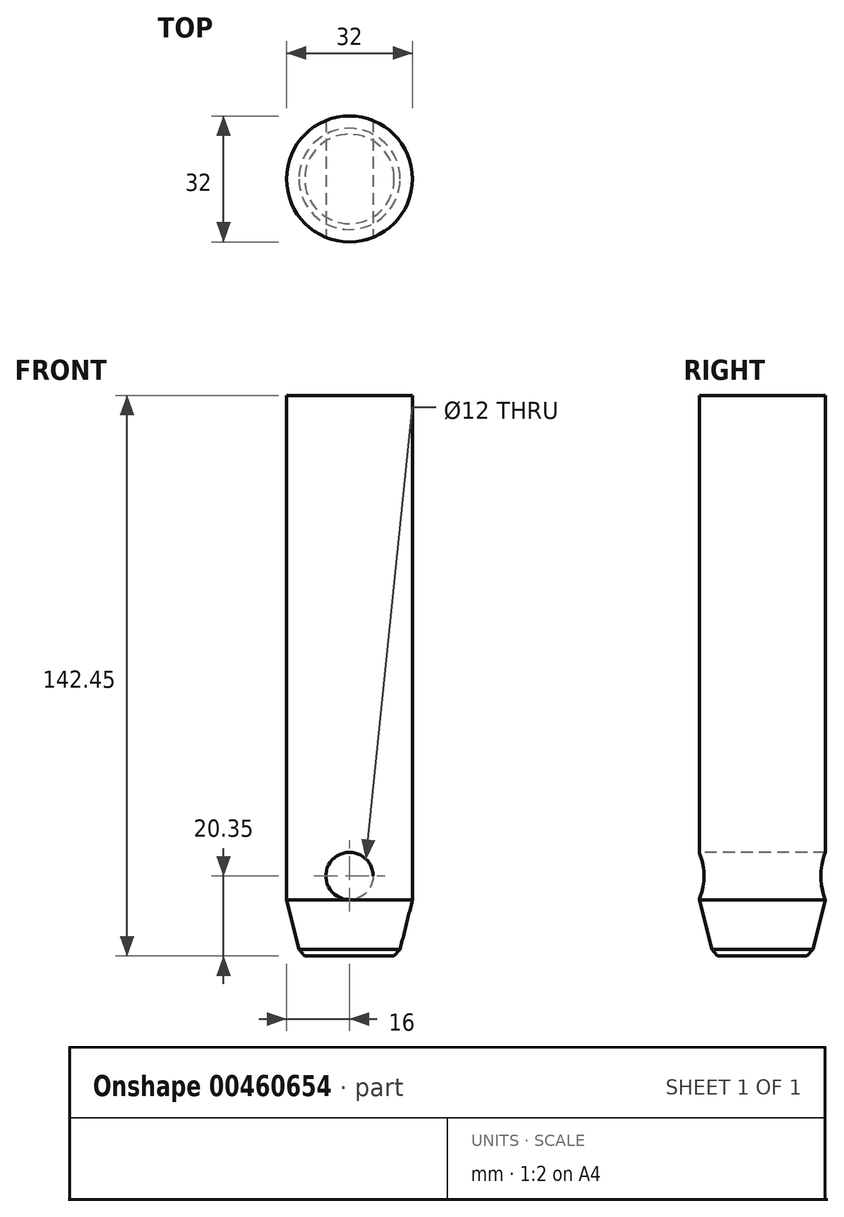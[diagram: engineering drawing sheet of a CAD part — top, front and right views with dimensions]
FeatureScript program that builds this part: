
annotation { "Feature Type Name" : "Feature", "Feature Type Description" : "" }
export const myFeature = defineFeature(function(context is Context, id is Id, definition is map)
    precondition{}
    {
        {
            var Q0;
            Q0=qCreatedBy(makeId("Front.planeOp"),FACE);
            var sketch = newSketch(context, id + "F0", { "sketchPlane" : qUnion([Q0])});
            skLineSegment(sketch, "E0.bottom", {"start": v(16, -71) * mm, "end": v(-16, -71) * mm});
            skLineSegment(sketch, "E0.top", {"start": v(16, 71) * mm, "end": v(-16, 71) * mm});
            skLineSegment(sketch, "E0.left", {"start": v(16, -71) * mm, "end": v(16, 71) * mm});
            skLineSegment(sketch, "E0.right", {"start": v(-16, -71) * mm, "end": v(-16, 71) * mm});
            skPoint(sketch, "E0.middle", {"position": v(0, 0) * mm});
            skLineSegment(sketch, "E1.0", {"start": v(16, -69.5) * mm, "end": v(-16, -69.5) * mm});
            skLineSegment(sketch, "E2.0", {"start": v(16, -57) * mm, "end": v(-16, -57) * mm});
            skLineSegment(sketch, "E3.0", {"start": v(16, -51) * mm, "end": v(-16, -51) * mm});
            skLineSegment(sketch, "E4", {"start": v(0, -49.32) * mm, "end": v(0, -53.2) * mm});
            skPoint(sketch, "E4.startSnap0", {"position": v(0, -51) * mm});
            skSolve(sketch);
        }
        {
            var Q0;
            Q0=qCreatedBy(makeId("Top.planeOp"),FACE);
            var sketch = newSketch(context, id + "F1", { "sketchPlane" : qUnion([Q0])});
            skCircle(sketch, "E5", {"center": v(0, 0) * mm, "radius": 16 * mm});
            skSolve(sketch);
        }
        {
            var Q0;
            Q0 = qSketchRegion(id + "F1", true);
            extrude(context, id + "F2", {"entities" : qUnion([Q0]), "depth" : 71.1 * mm});
        }
        {
            var Q0;
            Q0=makeQuery(id+"F2.opExtrude","CAP_FACE",FACE,{"disambiguationData":[OSD([sQuery(id+"F1.wireOp",EDGE,"E5")])],"isStart":true});
            extrude(context, id + "F3", {"entities" : qUnion([Q0]), "operationType" : NewBodyOperationType.ADD, "depth" : 57.1 * mm});
        }
        {
            var Q0;
            Q0=makeQuery(id+"F3.opExtrude","CAP_FACE",FACE,{"disambiguationData":[OSD([sQuery(id+"F1.wireOp",EDGE,"E5")])],"isStart":false});
            cPlane(context, id + "F4", {"entities" : qUnion([Q0]), "cplaneType" : CPlaneType.OFFSET, "offset" : 12.5 * mm, "width" : 150 * mm, "height" : 150 * mm});
        }
        {
            var Q0;
            Q0=qCreatedBy(id+"F4.planeOp",FACE);
            var sketch = newSketch(context, id + "F5", { "sketchPlane" : qUnion([Q0])});
            skCircle(sketch, "E6", {"center": v(0, 0) * mm, "radius": 12.85 * mm});
            skSolve(sketch);
        }
        {
            var Q1;
            Q1=makeQuery(id+"F3.opExtrude","CAP_FACE",FACE,{"disambiguationData":[OSD([sQuery(id+"F1.wireOp",EDGE,"E5")])],"isStart":false});
            var Q2;
            Q2=makeQuery(id+"F5.imprint","IMPRINT",FACE,{"disambiguationData":[TD([[makeQuery(id+"F5.imprint","IMPRINT",EDGE,{"derivedFrom":sQuery(id+"F5.wireOp",EDGE,"E6")}),1.0]])]});
            loft(context, id + "F6", {"operationType" : NewBodyOperationType.ADD, "sheetProfilesArray" : [{ "sheetProfileEntities" : qUnion([Q1]) }, { "sheetProfileEntities" : qUnion([Q2]) }]});
        }
        {
            var Q0;
            Q0=makeQuery(id+"F6.opLoft","CAP_FACE",FACE,{"disambiguationData":[OSD([makeQuery(id+"F5.imprint","IMPRINT",FACE,{"disambiguationData":[TD([[makeQuery(id+"F5.imprint","IMPRINT",EDGE,{"derivedFrom":sQuery(id+"F5.wireOp",EDGE,"E6")}),1.0]])]})])],"isStart":true});
            cPlane(context, id + "F7", {"entities" : qUnion([Q0]), "cplaneType" : CPlaneType.OFFSET, "offset" : 1.75 * mm, "width" : 150 * mm, "height" : 150 * mm});
        }
        {
            var Q0;
            Q0=qCreatedBy(id+"F7.planeOp",FACE);
            var sketch = newSketch(context, id + "F8", { "sketchPlane" : qUnion([Q0])});
            skCircle(sketch, "E7", {"center": v(0, 0) * mm, "radius": 11.38 * mm});
            skSolve(sketch);
        }
        {
            var Q1;
            Q1=makeQuery(id+"F8.imprint","IMPRINT",FACE,{"disambiguationData":[TD([[makeQuery(id+"F8.imprint","IMPRINT",EDGE,{"derivedFrom":sQuery(id+"F8.wireOp",EDGE,"E7")}),1.0]])]});
            var Q2;
            Q2=makeQuery(id+"F6.opLoft","CAP_FACE",FACE,{"disambiguationData":[OSD([makeQuery(id+"F5.imprint","IMPRINT",FACE,{"disambiguationData":[TD([[makeQuery(id+"F5.imprint","IMPRINT",EDGE,{"derivedFrom":sQuery(id+"F5.wireOp",EDGE,"E6")}),1.0]])]})])],"isStart":true});
            loft(context, id + "F9", {"operationType" : NewBodyOperationType.ADD, "sheetProfilesArray" : [{ "sheetProfileEntities" : qUnion([Q1]) }, { "sheetProfileEntities" : qUnion([Q2]) }]});
        }
        {
            var Q0;
            Q0=sQuery(id+"F0.wireOp",VERTEX,"E4.startSnap0");
            var Q1;
            Q1=makeQuery(id+"F2.opExtrude","SWEPT_BODY",BODY,{"disambiguationData":[OSD([sQuery(id+"F1.wireOp",EDGE,"E5")])]});
            hole(context, id + "F10", {"style" : HoleStyle.SIMPLE, "endStyle" : HoleEndStyle.THROUGH, "holeDiameter" : 12 * mm, "isTappedThrough" : true, "tappedDepth" : 12 * mm, "tapClearance" : 3, "locations" : qUnion([Q0]), "scope" : qUnion([Q1])});
        }
        {
            var Q0;
            Q0=qCreatedBy(makeId("Front.planeOp"),FACE);
            var sketch = newSketch(context, id + "F11", { "sketchPlane" : qUnion([Q0])});
            skLineSegment(sketch, "E8.bottom", {"start": v(16, -71) * mm, "end": v(-16, -71) * mm});
            skLineSegment(sketch, "E8.top", {"start": v(16, 71) * mm, "end": v(-16, 71) * mm});
            skLineSegment(sketch, "E8.left", {"start": v(16, -71) * mm, "end": v(16, 71) * mm});
            skLineSegment(sketch, "E8.right", {"start": v(-16, -71) * mm, "end": v(-16, 71) * mm});
            skPoint(sketch, "E8.middle", {"position": v(0, 0) * mm});
            skLineSegment(sketch, "E9.0", {"start": v(16, -69.5) * mm, "end": v(-16, -69.5) * mm});
            skLineSegment(sketch, "E10.0", {"start": v(16, -57) * mm, "end": v(-16, -57) * mm});
            skLineSegment(sketch, "E11.0", {"start": v(16, -51) * mm, "end": v(-16, -51) * mm});
            skLineSegment(sketch, "E12", {"start": v(0, -49.32) * mm, "end": v(0, -53.2) * mm});
            skPoint(sketch, "E12.startSnap0", {"position": v(0, -51) * mm});
            skSolve(sketch);
        }
        {
            var Q0;
            Q0=sQuery(id+"F11.wireOp",VERTEX,"E12.startSnap0");
            var Q1;
            Q1=makeQuery(id+"F2.opExtrude","SWEPT_BODY",BODY,{"disambiguationData":[OSD([sQuery(id+"F1.wireOp",EDGE,"E5")])]});
            hole(context, id + "F12", {"style" : HoleStyle.SIMPLE, "endStyle" : HoleEndStyle.THROUGH, "oppositeDirection" : true, "holeDiameter" : 12 * mm, "isTappedThrough" : true, "tappedDepth" : 12 * mm, "tapClearance" : 3, "locations" : qUnion([Q0]), "scope" : qUnion([Q1])});
        }
    });
